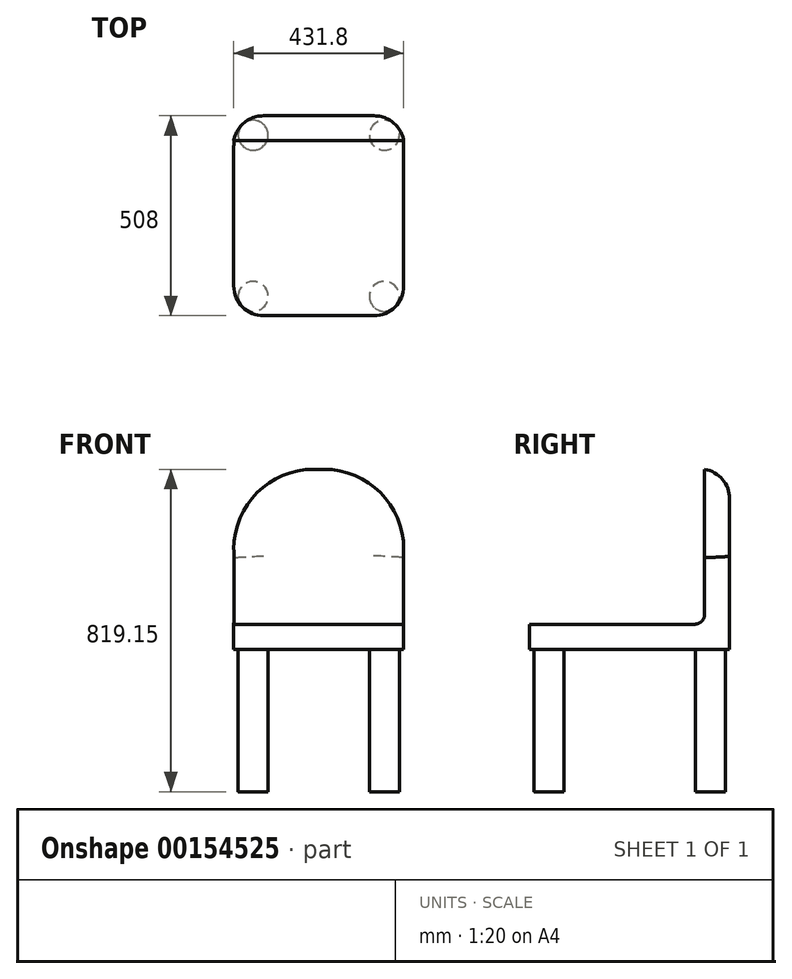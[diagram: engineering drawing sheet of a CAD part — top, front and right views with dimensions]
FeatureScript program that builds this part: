
annotation { "Feature Type Name" : "Feature", "Feature Type Description" : "" }
export const myFeature = defineFeature(function(context is Context, id is Id, definition is map)
    precondition{}
    {
        {
            var Q0;
            Q0=qCreatedBy(makeId("Top.planeOp"),FACE);
            var sketch = newSketch(context, id + "F0", { "sketchPlane" : qUnion([Q0])});
            skLineSegment(sketch, "E0.bottom", {"start": v(215.9, 254) * mm, "end": v(-215.9, 254) * mm});
            skLineSegment(sketch, "E0.top", {"start": v(215.9, -254) * mm, "end": v(-215.9, -254) * mm});
            skLineSegment(sketch, "E0.left", {"start": v(215.9, 254) * mm, "end": v(215.9, -254) * mm});
            skLineSegment(sketch, "E0.right", {"start": v(-215.9, 254) * mm, "end": v(-215.9, -254) * mm});
            skPoint(sketch, "E0.middle", {"position": v(0, 0) * mm});
            skSolve(sketch);
        }
        {
            var Q0;
            Q0=makeQuery(id+"F0.imprint","IMPRINT",FACE,{"disambiguationData":[TD([[makeQuery(id+"F0.imprint","IMPRINT",EDGE,{"derivedFrom":sQuery(id+"F0.wireOp",EDGE,"E0.bottom")}),1.0]])]});
            extrude(context, id + "F1", {"entities" : qUnion([Q0]), "depth" : 63.5 * mm});
        }
        {
            var Q0;
            Q0=makeQuery(id+"F1.opExtrude","SWEPT_FACE",FACE,{"disambiguationData":[OSD([sQuery(id+"F0.wireOp",EDGE,"E0.bottom")])]});
            var sketch = newSketch(context, id + "F2", { "sketchPlane" : qUnion([Q0])});
            skLineSegment(sketch, "E1.bottom", {"start": v(-215.9, 0) * mm, "end": v(215.9, 0) * mm});
            skLineSegment(sketch, "E1.top", {"start": v(-215.9, 457.2) * mm, "end": v(215.9, 457.2) * mm});
            skLineSegment(sketch, "E1.left", {"start": v(-215.9, 0) * mm, "end": v(-215.9, 457.2) * mm});
            skLineSegment(sketch, "E1.right", {"start": v(215.9, 0) * mm, "end": v(215.9, 457.2) * mm});
            skSolve(sketch);
        }
        {
            var Q0;
            {var subQ0=sQuery(id+"F2.wireOp",EDGE,"E1.top");Q0=makeQuery(id+"F2.imprint","IMPRINT",FACE,{"disambiguationData":[TD([[makeQuery(id+"F2.imprint","IMPRINT",EDGE,{"derivedFrom":subQ0}),-1.0]])]});}
            var Q1;
            {var subQ0=sQuery(id+"F2.wireOp",EDGE,"E1.bottom");Q1=makeQuery(id+"F2.imprint","IMPRINT",FACE,{"disambiguationData":[TD([[makeQuery(id+"F2.imprint","IMPRINT",EDGE,{"derivedFrom":subQ0}),1.0]])]});}
            extrude(context, id + "F3", {"entities" : qUnion([Q0, Q1]), "operationType" : NewBodyOperationType.ADD, "oppositeDirection" : true, "depth" : 63.5 * mm});
        }
        {
            var Q0;
            Q0=makeQuery(id+"F3.opExtrude","SWEPT_EDGE",EDGE,{"disambiguationData":[OSD([sQuery(id+"F2.wireOp",EDGE,"E1.top"),sQuery(id+"F2.wireOp",EDGE,"E1.left")])]});
            var Q1;
            Q1=makeQuery(id+"F3.opExtrude","SWEPT_EDGE",EDGE,{"disambiguationData":[OSD([sQuery(id+"F2.wireOp",EDGE,"E1.top"),sQuery(id+"F2.wireOp",EDGE,"E1.right")])]});
            fillet(context, id + "F4", {"entities" : qUnion([Q0, Q1]), "radius" : 203.2 * mm, "tangentPropagation" : true, "allowEdgeOverflow" : false});
        }
        {
            var Q0;
            Q0=makeQuery(id+"F1.opExtrude","SWEPT_EDGE",EDGE,{"disambiguationData":[OSD([sQuery(id+"F0.wireOp",EDGE,"E0.top"),sQuery(id+"F0.wireOp",EDGE,"E0.right")])]});
            var Q1;
            Q1=makeQuery(id+"F1.opExtrude","SWEPT_EDGE",EDGE,{"disambiguationData":[OSD([sQuery(id+"F0.wireOp",EDGE,"E0.top"),sQuery(id+"F0.wireOp",EDGE,"E0.left")])]});
            var Q2;
            Q2=makeQuery(id+"F1.opExtrude","SWEPT_EDGE",EDGE,{"disambiguationData":[OSD([sQuery(id+"F0.wireOp",EDGE,"E0.bottom"),sQuery(id+"F0.wireOp",EDGE,"E0.left")])]});
            var Q3;
            Q3=makeQuery(id+"F1.opExtrude","SWEPT_EDGE",EDGE,{"disambiguationData":[OSD([sQuery(id+"F0.wireOp",EDGE,"E0.bottom"),sQuery(id+"F0.wireOp",EDGE,"E0.right")])]});
            fillet(context, id + "F5", {"entities" : qUnion([Q0, Q1, Q2, Q3]), "radius" : 76.2 * mm, "tangentPropagation" : true, "allowEdgeOverflow" : false});
        }
        {
            var Q0;
            Q0=makeQuery(id+"F1.opExtrude","CAP_FACE",FACE,{"disambiguationData":[OSD([sQuery(id+"F0.wireOp",EDGE,"E0.bottom"),sQuery(id+"F0.wireOp",EDGE,"E0.top"),sQuery(id+"F0.wireOp",EDGE,"E0.left"),sQuery(id+"F0.wireOp",EDGE,"E0.right")])],"isStart":true});
            var sketch = newSketch(context, id + "F6", { "sketchPlane" : qUnion([Q0])});
            skCircle(sketch, "E2", {"center": v(166.64, 204.74) * mm, "radius": 38.1 * mm});
            skCircle(sketch, "E3", {"center": v(-166.64, 204.74) * mm, "radius": 38.1 * mm});
            skCircle(sketch, "E4", {"center": v(166.64, -204.74) * mm, "radius": 38.1 * mm});
            skCircle(sketch, "E5", {"center": v(-166.64, -204.74) * mm, "radius": 38.1 * mm});
            skLineSegment(sketch, "E6", {"start": v(193.58, 231.68) * mm, "end": v(166.64, 204.74) * mm, "construction": true});
            skSolve(sketch);
        }
        {
            var Q0;
            Q0 = qSketchRegion(id + "F6", true);
            extrude(context, id + "F7", {"entities" : qUnion([Q0]), "operationType" : NewBodyOperationType.ADD, "depth" : 361.95 * mm});
        }
        {
            var Q0;
            Q0=makeQuery(id+"F7.opExtrude","CAP_EDGE",EDGE,{"disambiguationData":[OSD([sQuery(id+"F6.wireOp",EDGE,"E5")])],"isStart":true});
            var Q1;
            Q1=makeQuery(id+"F7.opExtrude","CAP_EDGE",EDGE,{"disambiguationData":[OSD([sQuery(id+"F6.wireOp",EDGE,"E3")])],"isStart":true});
            var Q2;
            Q2=makeQuery(id+"F7.opExtrude","CAP_EDGE",EDGE,{"disambiguationData":[OSD([sQuery(id+"F6.wireOp",EDGE,"E2")])],"isStart":true});
            var Q3;
            Q3=makeQuery(id+"F7.opExtrude","CAP_EDGE",EDGE,{"disambiguationData":[OSD([sQuery(id+"F6.wireOp",EDGE,"E4")])],"isStart":true});
            var Q4;
            Q4=makeQuery(id+"F3.boolean.opBoolean","INTERSECT",EDGE,{"derivedFrom":[makeQuery(id+"F1.opExtrude","CAP_FACE",FACE,{"disambiguationData":[OSD([sQuery(id+"F0.wireOp",EDGE,"E0.bottom"),sQuery(id+"F0.wireOp",EDGE,"E0.top"),sQuery(id+"F0.wireOp",EDGE,"E0.left"),sQuery(id+"F0.wireOp",EDGE,"E0.right")])],"isStart":false}),makeQuery(id+"F3.opExtrude","CAP_FACE",FACE,{"disambiguationData":[OSD([sQuery(id+"F2.wireOp",EDGE,"E1.bottom"),sQuery(id+"F2.wireOp",EDGE,"E1.top"),sQuery(id+"F2.wireOp",EDGE,"E1.left"),sQuery(id+"F2.wireOp",EDGE,"E1.right")])],"isStart":false})]});
            fillet(context, id + "F8", {"entities" : qUnion([Q0, Q1, Q2, Q3, Q4]), "radius" : 25.4 * mm, "tangentPropagation" : true, "allowEdgeOverflow" : false});
        }
    });
